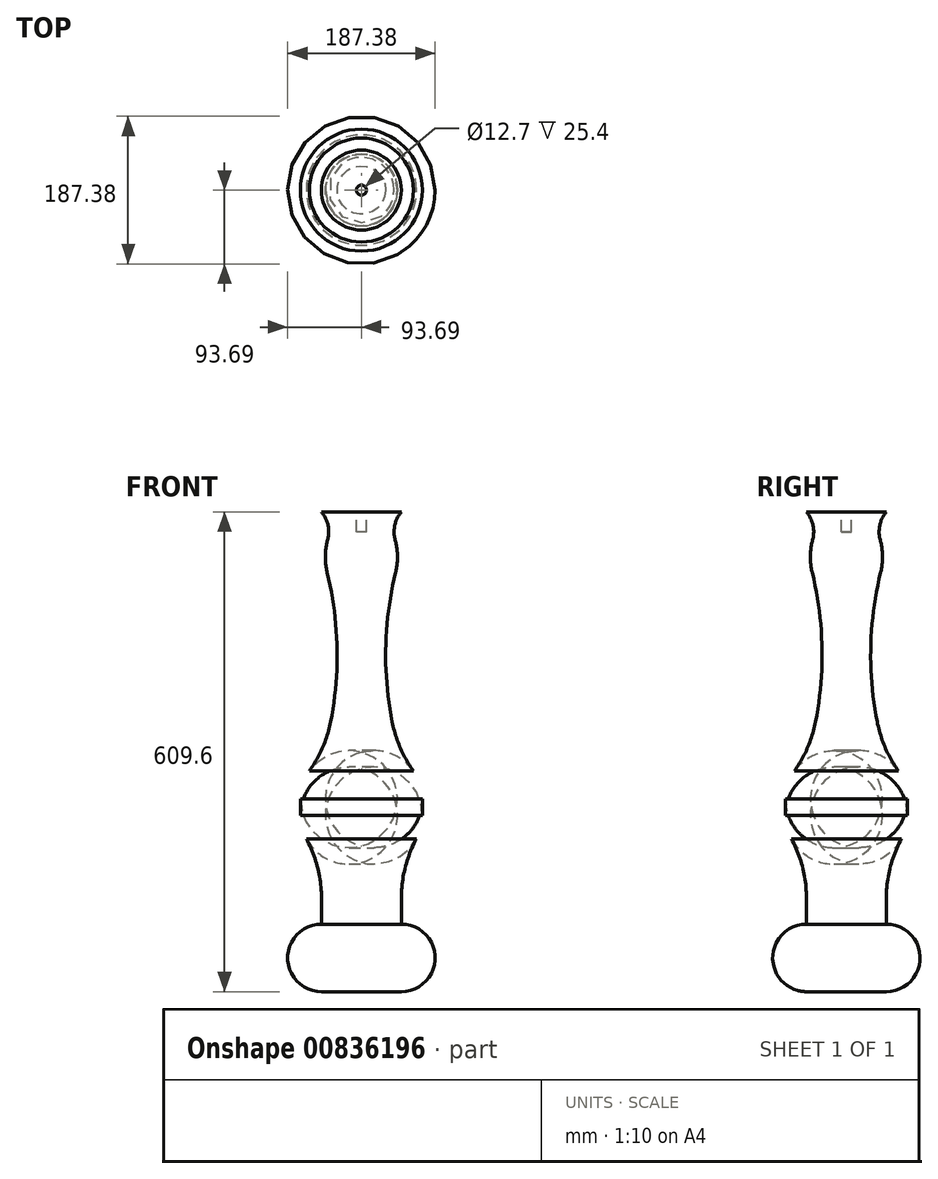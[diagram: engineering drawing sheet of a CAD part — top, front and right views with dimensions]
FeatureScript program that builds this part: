
annotation { "Feature Type Name" : "Feature", "Feature Type Description" : "" }
export const myFeature = defineFeature(function(context is Context, id is Id, definition is map)
    precondition{}
    {
        {
            var Q0;
            Q0=qCreatedBy(makeId("Front.planeOp"),FACE);
            var sketch = newSketch(context, id + "F0", { "sketchPlane" : qUnion([Q0])});
            skLineSegment(sketch, "E0", {"start": v(0, 312.8) * mm, "end": v(0, -296.8) * mm});
            skLineSegment(sketch, "E1", {"start": v(50.8, -296.8) * mm, "end": v(0, -296.8) * mm});
            skArc(sketch, "E2", {"start": v(50.8, 262) * mm, "mid": v(30.83, 131) * mm, "end": v(50.8, 0) * mm});
            skLineSegment(sketch, "E3", {"start": v(50.8, 0) * mm, "end": v(113.43, -62.63) * mm});
            skLineSegment(sketch, "E4", {"start": v(113.43, -62.63) * mm, "end": v(50.8, -125.26) * mm});
            skArc(sketch, "E5", {"start": v(50.8, -296.8) * mm, "mid": v(93.69, -253.92) * mm, "end": v(50.8, -211.03) * mm});
            skLineSegment(sketch, "E6.trimOffspring", {"start": v(50.8, -211.03) * mm, "end": v(50.8, -125.26) * mm});
            skLineSegment(sketch, "E7", {"start": v(0, 312.8) * mm, "end": v(50.8, 312.8) * mm});
            skArc(sketch, "E8", {"start": v(50.8, 312.8) * mm, "mid": v(41.53, 287.4) * mm, "end": v(50.8, 262) * mm});
            skSolve(sketch);
        }
        {
            var Q0;
            Q0=makeQuery(id+"F0.imprint","IMPRINT",FACE,{"disambiguationData":[TD([[makeQuery(id+"F0.imprint","IMPRINT",EDGE,{"derivedFrom":sQuery(id+"F0.wireOp",EDGE,"E0")}),1.0]])]});
            var Q1;
            Q1=sQuery(id+"F0.wireOp",EDGE,"E0");
            revolve(context, id + "F1", {"surfaceOperationType" : NewSurfaceOperationType.NEW, "entities" : qUnion([Q0]), "axis" : qUnion([Q1]), "revolveType" : RevolveType.FULL});
        }
        {
            var Q0;
            Q0=makeQuery(id+"F1.opRevolve","SWEPT_EDGE",EDGE,{"disambiguationData":[OSD([sQuery(id+"F0.wireOp",EDGE,"E3"),sQuery(id+"F0.wireOp",EDGE,"E4")])]});
            chamfer(context, id + "F2", {"entities" : qUnion([Q0]), "width" : 50.8 * mm, "tangentPropagation" : true});
        }
        {
            var Q0;
            {var subQ0=sQuery(id+"F0.wireOp",EDGE,"E3");Q0=makeQuery(id+"F2.opChamfer","BLEND_EDGE",EDGE,{"blendedFrom":[makeQuery(id+"F1.opRevolve","SWEPT_EDGE",EDGE,{"disambiguationData":[OSD([subQ0,sQuery(id+"F0.wireOp",EDGE,"E4")])]}),makeQuery(id+"F1.opRevolve","SWEPT_FACE",FACE,{"disambiguationData":[OSD([subQ0])]})],"blendedInto":[makeQuery(id+"F1.opRevolve","SWEPT_FACE",FACE,{"disambiguationData":[OSD([subQ0])]})]});}
            var Q1;
            {var subQ0=sQuery(id+"F0.wireOp",EDGE,"E4");Q1=makeQuery(id+"F2.opChamfer","BLEND_EDGE",EDGE,{"blendedFrom":[makeQuery(id+"F1.opRevolve","SWEPT_EDGE",EDGE,{"disambiguationData":[OSD([sQuery(id+"F0.wireOp",EDGE,"E3"),subQ0])]}),makeQuery(id+"F1.opRevolve","SWEPT_FACE",FACE,{"disambiguationData":[OSD([subQ0])]})],"blendedInto":[makeQuery(id+"F1.opRevolve","SWEPT_FACE",FACE,{"disambiguationData":[OSD([subQ0])]})]});}
            fillet(context, id + "F3", {"entities" : qUnion([Q0, Q1]), "radius" : 61.66 * mm, "tangentPropagation" : true, "allowEdgeOverflow" : false});
        }
        {
            var Q0;
            Q0=makeQuery(id+"F1.opRevolve","SWEPT_EDGE",EDGE,{"disambiguationData":[OSD([sQuery(id+"F0.wireOp",EDGE,"E2"),sQuery(id+"F0.wireOp",EDGE,"E3")])]});
            fillet(context, id + "F4", {"entities" : qUnion([Q0]), "radius" : 161.6 * mm, "tangentPropagation" : true, "allowEdgeOverflow" : false});
        }
        {
            var Q0;
            Q0=makeQuery(id+"F1.opRevolve","SWEPT_EDGE",EDGE,{"disambiguationData":[OSD([sQuery(id+"F0.wireOp",EDGE,"E4"),sQuery(id+"F0.wireOp",EDGE,"E6.trimOffspring")])]});
            fillet(context, id + "F5", {"entities" : qUnion([Q0]), "radius" : 157.22 * mm, "tangentPropagation" : true, "allowEdgeOverflow" : false});
        }
        {
            var Q0;
            Q0=makeQuery(id+"F1.opRevolve","SWEPT_EDGE",EDGE,{"disambiguationData":[OSD([sQuery(id+"F0.wireOp",EDGE,"E2"),sQuery(id+"F0.wireOp",EDGE,"E8")])]});
            fillet(context, id + "F6", {"entities" : qUnion([Q0]), "radius" : 83.32 * mm, "tangentPropagation" : true, "allowEdgeOverflow" : false});
        }
        {
            var Q0;
            Q0=makeQuery(id+"F1.opRevolve","SWEPT_FACE",FACE,{"disambiguationData":[OSD([sQuery(id+"F0.wireOp",EDGE,"E7")])]});
            var sketch = newSketch(context, id + "F7", { "sketchPlane" : qUnion([Q0])});
            skCircle(sketch, "E9", {"center": v(0, 0) * mm, "radius": 6.35 * mm});
            skSolve(sketch);
        }
        {
            var Q0;
            Q0 = qSketchRegion(id + "F7", true);
            extrude(context, id + "F8", {"entities" : qUnion([Q0]), "operationType" : NewBodyOperationType.REMOVE, "oppositeDirection" : true, "depth" : 25.4 * mm, "offsetDistance" : 25.4 * mm});
        }
    });
